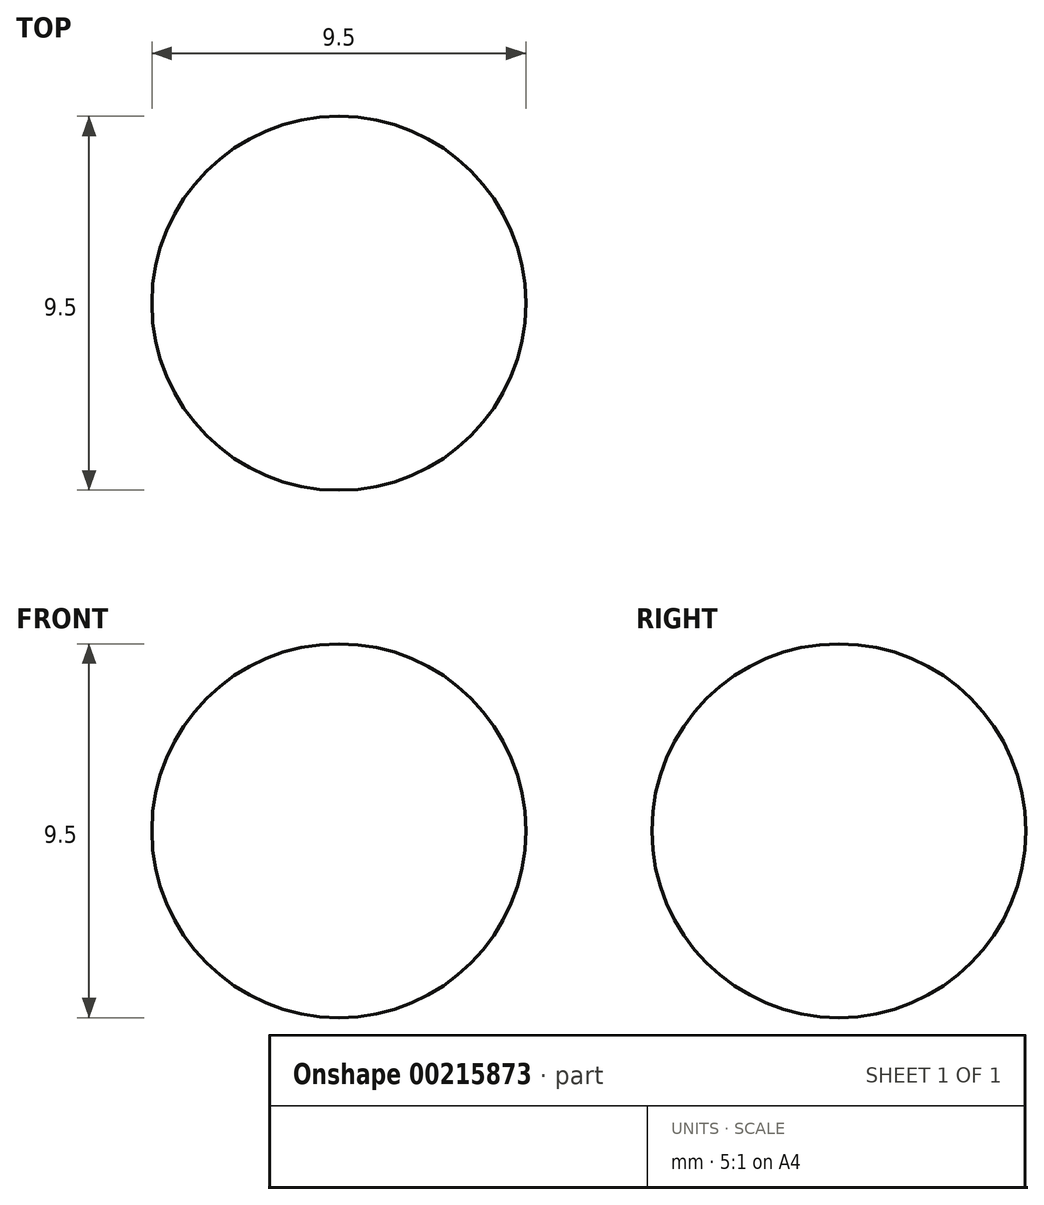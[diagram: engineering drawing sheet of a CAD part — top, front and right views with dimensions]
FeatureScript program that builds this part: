
annotation { "Feature Type Name" : "Feature", "Feature Type Description" : "" }
export const myFeature = defineFeature(function(context is Context, id is Id, definition is map)
    precondition{}
    {
        {
            var Q0;
            Q0=qCreatedBy(makeId("Front.planeOp"),FACE);
            var sketch = newSketch(context, id + "F0", { "sketchPlane" : qUnion([Q0])});
            skArc(sketch, "E0", {"start": v(9.93, -4.9) * mm, "mid": v(14.68, -0.14) * mm, "end": v(9.93, 4.6) * mm});
            skLineSegment(sketch, "E1", {"start": v(9.93, -0.14) * mm, "end": v(9.93, 4.6) * mm});
            skLineSegment(sketch, "E2", {"start": v(9.93, -0.14) * mm, "end": v(9.93, -4.9) * mm});
            skSolve(sketch);
        }
        {
            var Q0;
            Q0=makeQuery(id+"F0.imprint","IMPRINT",FACE,{"disambiguationData":[TD([[makeQuery(id+"F0.imprint","IMPRINT",EDGE,{"derivedFrom":sQuery(id+"F0.wireOp",EDGE,"E0")}),1.0]])]});
            var Q1;
            Q1=sQuery(id+"F0.wireOp",EDGE,"E1");
            revolve(context, id + "F1", {"entities" : qUnion([Q0]), "axis" : qUnion([Q1]), "revolveType" : RevolveType.FULL});
        }
    });
